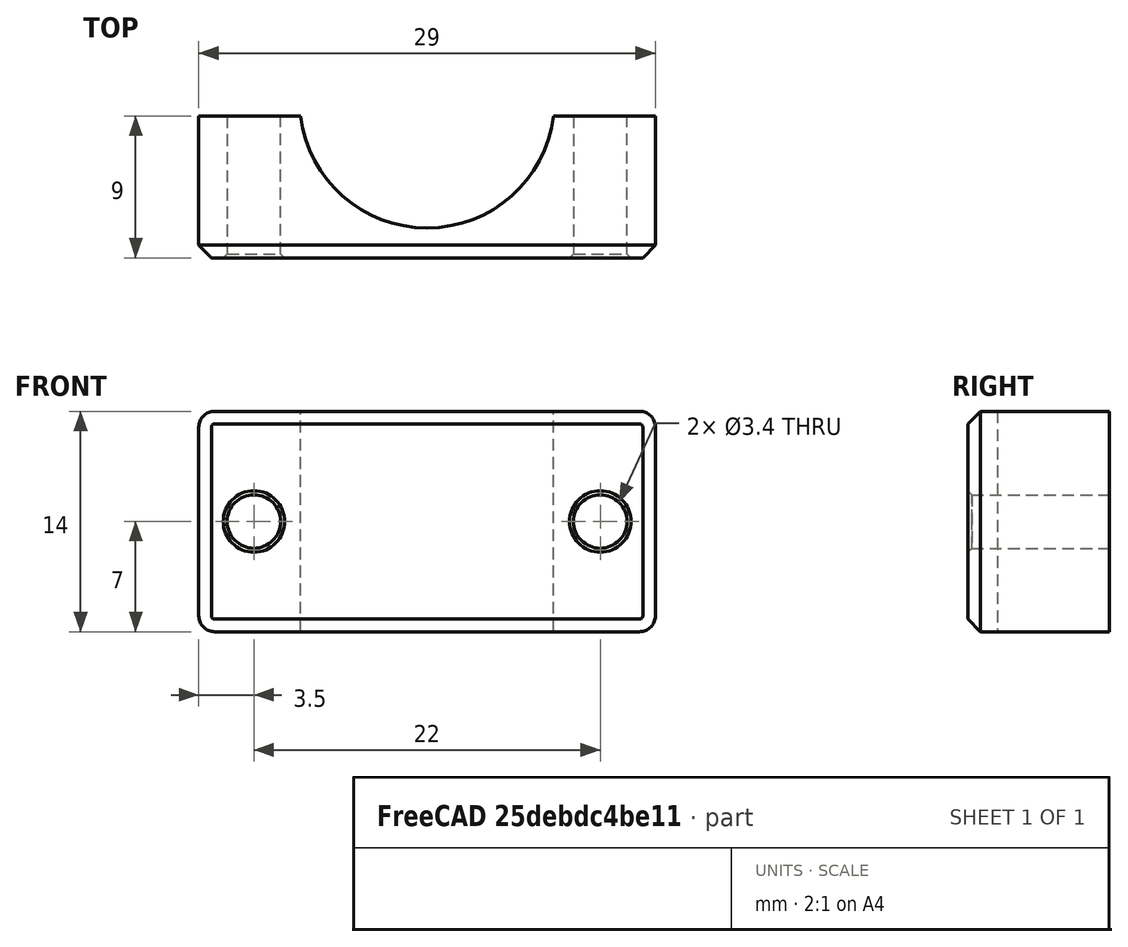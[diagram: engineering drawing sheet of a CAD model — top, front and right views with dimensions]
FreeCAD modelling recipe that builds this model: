
FCSTD DOCUMENT  (FreeCAD 0.19R)
Label: HeadClamp
License: All rights reserved
LicenseURL: http://en.wikipedia.org/wiki/All_rights_reserved
objects: Sketcher::SketchObject×2, PartDesign::Chamfer×2, PartDesign::Pad×1, PartDesign::Pocket×1, PartDesign::Fillet×1, PartDesign::Body×1, Mesh::Feature×1
note: 13 computed .brp shape members not serialized (recipe doc carries the construction recipe); baked Part::Feature solids carry a one-line shape summary decoded from their .brp

FEATURE [Sketcher::SketchObject] Sketch
  FullyConstrained = true
  MapMode = 5
  Support = -> [XY_Plane]
  sketch-geometry (6):
    g0: ArcOfCircle CenterX=0 CenterY=0 CenterZ=0 NormalX=0 NormalY=0 NormalZ=1 AngleXU=0 Radius=8.1 StartAngle=3.26537 EndAngle=6.15941
    g1: LineSegment StartX=8.03803 StartY=-1 StartZ=0 EndX=14.5 EndY=-1 EndZ=0
    g2: LineSegment StartX=14.5 StartY=-1 StartZ=0 EndX=14.5 EndY=-10 EndZ=0
    g3: LineSegment StartX=14.5 StartY=-10 StartZ=0 EndX=-14.5 EndY=-10 EndZ=0
    g4: LineSegment StartX=-14.5 StartY=-10 StartZ=0 EndX=-14.5 EndY=-1 EndZ=0
    g5: LineSegment StartX=-14.5 StartY=-1 StartZ=0 EndX=-8.03803 EndY=-1 EndZ=0
  constraints (17):
    c: Coincident(g0,g-1)
    c: Diameter(g0) = 16.2
    c: Horizontal(g1)
    c: Coincident(g1,g2)
    c: Vertical(g2)
    c: Coincident(g2,g3)
    c: Horizontal(g3)
    c: Coincident(g3,g4)
    c: Vertical(g4)
    c: Coincident(g4,g5)
    c: Horizontal(g5)
    c: DistanceY(g4) = -1
    c: Symmetric(g1,g4,g-2)
    c: Coincident(g0,g1)
    c: Coincident(g0,g5)
    c: Distance(g1,g4) = 29
    c: Distance(g2) = 9
FEATURE [PartDesign::Pad] Pad
  Direction = (1,1,1)
  Length = 14
  Length2 = 100
  Profile = -> Sketch
  Type = 0
FEATURE [Sketcher::SketchObject] Sketch001
  FullyConstrained = true
  MapMode = 5
  Placement = pos=(0,-1,0) rot=(0,0.707107,0.707107;3.14159rad)
  Support = -> [Pad]
  sketch-geometry (2):
    g0: Circle CenterX=-11 CenterY=7 CenterZ=0 NormalX=0 NormalY=0 NormalZ=1 AngleXU=0 Radius=1.7
    g1: Circle CenterX=11 CenterY=7 CenterZ=0 NormalX=0 NormalY=0 NormalZ=1 AngleXU=0 Radius=1.7
  constraints (5):
    c: Diameter(g1) = 3.4
    c: Equal(g1,g0)
    c: Symmetric(g1,g0,g-2)
    c: Distance(g1,g0) = 22
    c: DistanceY(g0) = 7
FEATURE [PartDesign::Pocket] Pocket
  BaseFeature = -> Pad
  Length = 5
  Length2 = 100
  Profile = -> Sketch001
  Type = 1
FEATURE [PartDesign::Fillet] Fillet
  Base = -> Pocket [Edge18,Edge16,Edge15,Edge13]
  BaseFeature = -> Pocket
  Radius = 1
  SupportTransform = false
FEATURE [PartDesign::Chamfer] Chamfer
  Angle = 45
  Base = -> Fillet [Edge22]
  BaseFeature = -> Fillet
  ChamferType = 0
  FlipDirection = false
  Size = 0.8
  Size2 = 1
  SupportTransform = false
FEATURE [PartDesign::Chamfer] Chamfer001
  Angle = 45
  Base = -> Chamfer [Edge32,Edge31]
  BaseFeature = -> Chamfer
  ChamferType = 0
  FlipDirection = false
  Size = 0.25
  Size2 = 1
  SupportTransform = false
FEATURE [PartDesign::Body] Body
  Group = -> [Sketch,Pad,Sketch001,Pocket,Fillet,Chamfer,Chamfer001]
  Origin = -> Origin
  Tip = -> Chamfer001
FEATURE [Mesh::Feature] Mesh  label="Chamfer001 (Meshed)"
